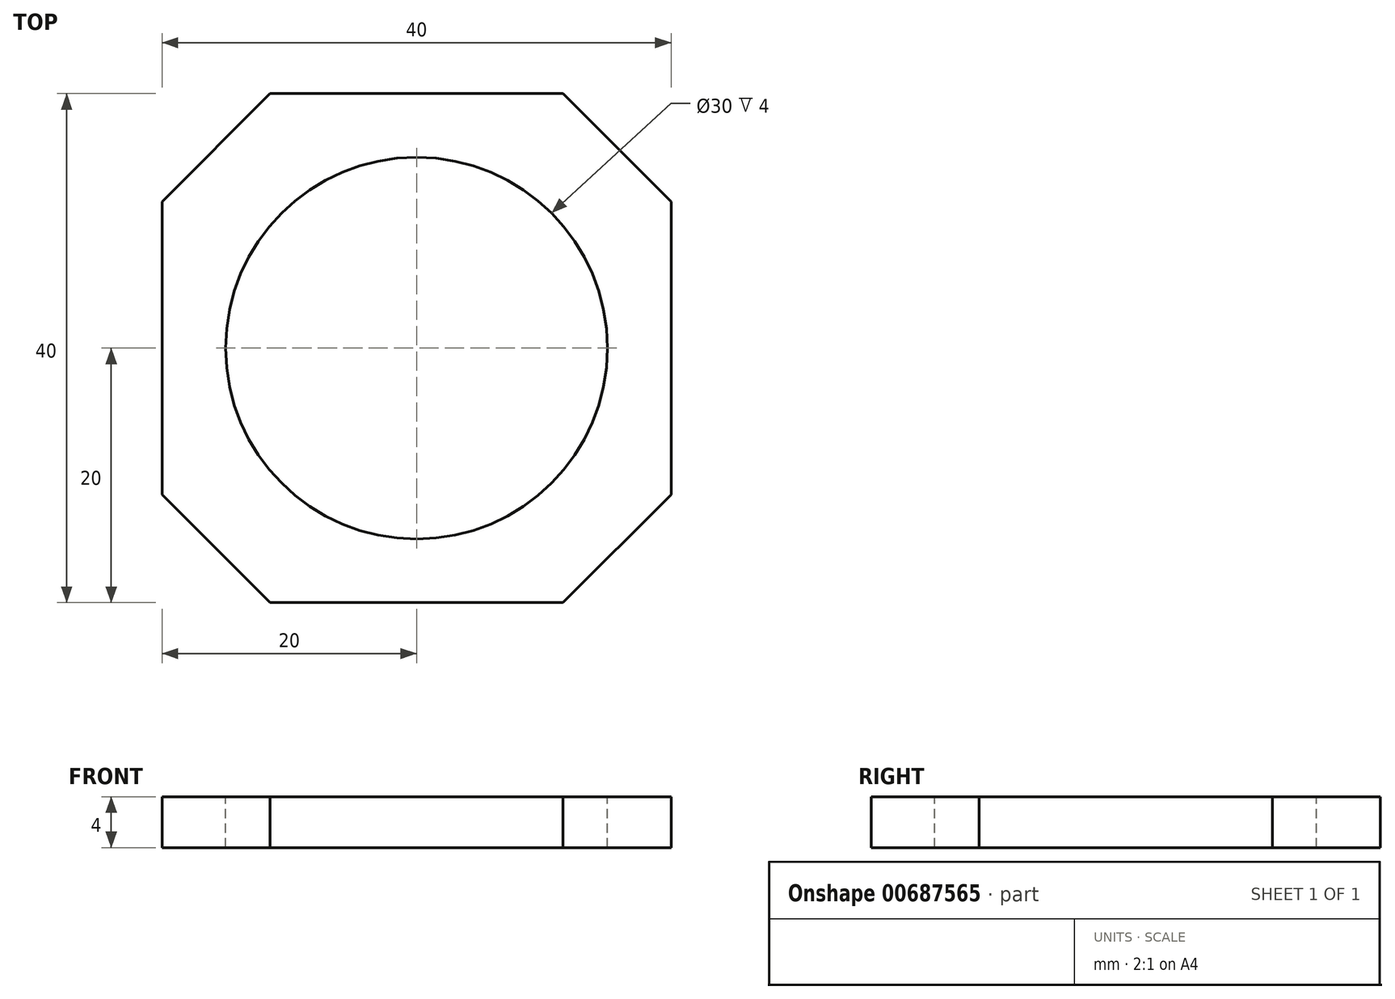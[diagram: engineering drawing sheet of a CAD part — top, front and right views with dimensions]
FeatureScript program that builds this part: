
annotation { "Feature Type Name" : "Feature", "Feature Type Description" : "" }
export const myFeature = defineFeature(function(context is Context, id is Id, definition is map)
    precondition{}
    {
        {
            var Q0;
            Q0=qCreatedBy(makeId("Top.planeOp"),FACE);
            var sketch = newSketch(context, id + "F0", { "sketchPlane" : qUnion([Q0])});
            skLineSegment(sketch, "E0.bottom", {"start": v(0, 0) * mm, "end": v(40, 0) * mm});
            skLineSegment(sketch, "E0.top", {"start": v(0, 40) * mm, "end": v(40, 40) * mm});
            skLineSegment(sketch, "E0.left", {"start": v(0, 0) * mm, "end": v(0, 40) * mm});
            skLineSegment(sketch, "E0.right", {"start": v(40, 0) * mm, "end": v(40, 40) * mm});
            skSolve(sketch);
        }
        {
            var Q0;
            Q0=makeQuery(id+"F0.imprint","IMPRINT",FACE,{"disambiguationData":[TD([[makeQuery(id+"F0.imprint","IMPRINT",EDGE,{"derivedFrom":sQuery(id+"F0.wireOp",EDGE,"E0.bottom")}),1.0]])]});
            extrude(context, id + "F1", {"entities" : qUnion([Q0]), "depth" : 4 * mm, "offsetDistance" : 25 * mm});
        }
        {
            var Q0;
            Q0=makeQuery(id+"F1.opExtrude","CAP_FACE",FACE,{"disambiguationData":[OSD([sQuery(id+"F0.wireOp",EDGE,"E0.bottom"),sQuery(id+"F0.wireOp",EDGE,"E0.top"),sQuery(id+"F0.wireOp",EDGE,"E0.left"),sQuery(id+"F0.wireOp",EDGE,"E0.right")])],"isStart":false});
            var sketch = newSketch(context, id + "F2", { "sketchPlane" : qUnion([Q0])});
            skLineSegment(sketch, "E1", {"start": v(0, 31.51) * mm, "end": v(8.49, 40) * mm});
            skLineSegment(sketch, "E2", {"start": v(31.51, 40) * mm, "end": v(40, 31.51) * mm});
            skLineSegment(sketch, "E3", {"start": v(0, 8.49) * mm, "end": v(8.49, 0) * mm});
            skLineSegment(sketch, "E4", {"start": v(40, 8.49) * mm, "end": v(31.51, 0) * mm});
            skSolve(sketch);
        }
        {
            var Q0;
            {var subQ0=sQuery(id+"F2.wireOp",EDGE,"E1");Q0=makeQuery(id+"F2.imprint","IMPRINT",FACE,{"disambiguationData":[TD([[makeQuery(id+"F2.imprint","IMPRINT",EDGE,{"derivedFrom":subQ0}),1.0]])]});}
            var Q1;
            {var subQ0=sQuery(id+"F2.wireOp",EDGE,"E2");Q1=makeQuery(id+"F2.imprint","IMPRINT",FACE,{"disambiguationData":[TD([[makeQuery(id+"F2.imprint","IMPRINT",EDGE,{"derivedFrom":subQ0}),1.0]])]});}
            var Q2;
            {var subQ0=sQuery(id+"F2.wireOp",EDGE,"E4");Q2=makeQuery(id+"F2.imprint","IMPRINT",FACE,{"disambiguationData":[TD([[makeQuery(id+"F2.imprint","IMPRINT",EDGE,{"derivedFrom":subQ0}),1.0]])]});}
            var Q3;
            {var subQ0=sQuery(id+"F2.wireOp",EDGE,"E3");Q3=makeQuery(id+"F2.imprint","IMPRINT",FACE,{"disambiguationData":[TD([[makeQuery(id+"F2.imprint","IMPRINT",EDGE,{"derivedFrom":subQ0}),-1.0]])]});}
            extrude(context, id + "F3", {"entities" : qUnion([Q0, Q1, Q2, Q3]), "operationType" : NewBodyOperationType.REMOVE, "oppositeDirection" : true, "depth" : 25 * mm, "offsetDistance" : 25 * mm});
        }
        {
            var Q0;
            Q0=makeQuery(id+"F1.opExtrude","CAP_FACE",FACE,{"disambiguationData":[OSD([sQuery(id+"F0.wireOp",EDGE,"E0.bottom"),sQuery(id+"F0.wireOp",EDGE,"E0.top"),sQuery(id+"F0.wireOp",EDGE,"E0.left"),sQuery(id+"F0.wireOp",EDGE,"E0.right")])],"isStart":false});
            var sketch = newSketch(context, id + "F4", { "sketchPlane" : qUnion([Q0])});
            skCircle(sketch, "E5", {"center": v(20, 20) * mm, "radius": 15 * mm});
            skPoint(sketch, "E5.centerSnap0", {"position": v(40, 20) * mm});
            skPoint(sketch, "E5.centerSnap1", {"position": v(20, 40) * mm});
            skSolve(sketch);
        }
        {
            var Q0;
            Q0=makeQuery(id+"F4.imprint","IMPRINT",FACE,{"disambiguationData":[TD([[makeQuery(id+"F4.imprint","IMPRINT",EDGE,{"derivedFrom":sQuery(id+"F4.wireOp",EDGE,"E5")}),1.0]])]});
            extrude(context, id + "F5", {"entities" : qUnion([Q0]), "operationType" : NewBodyOperationType.REMOVE, "oppositeDirection" : true, "depth" : 25 * mm, "offsetDistance" : 25 * mm});
        }
    });
